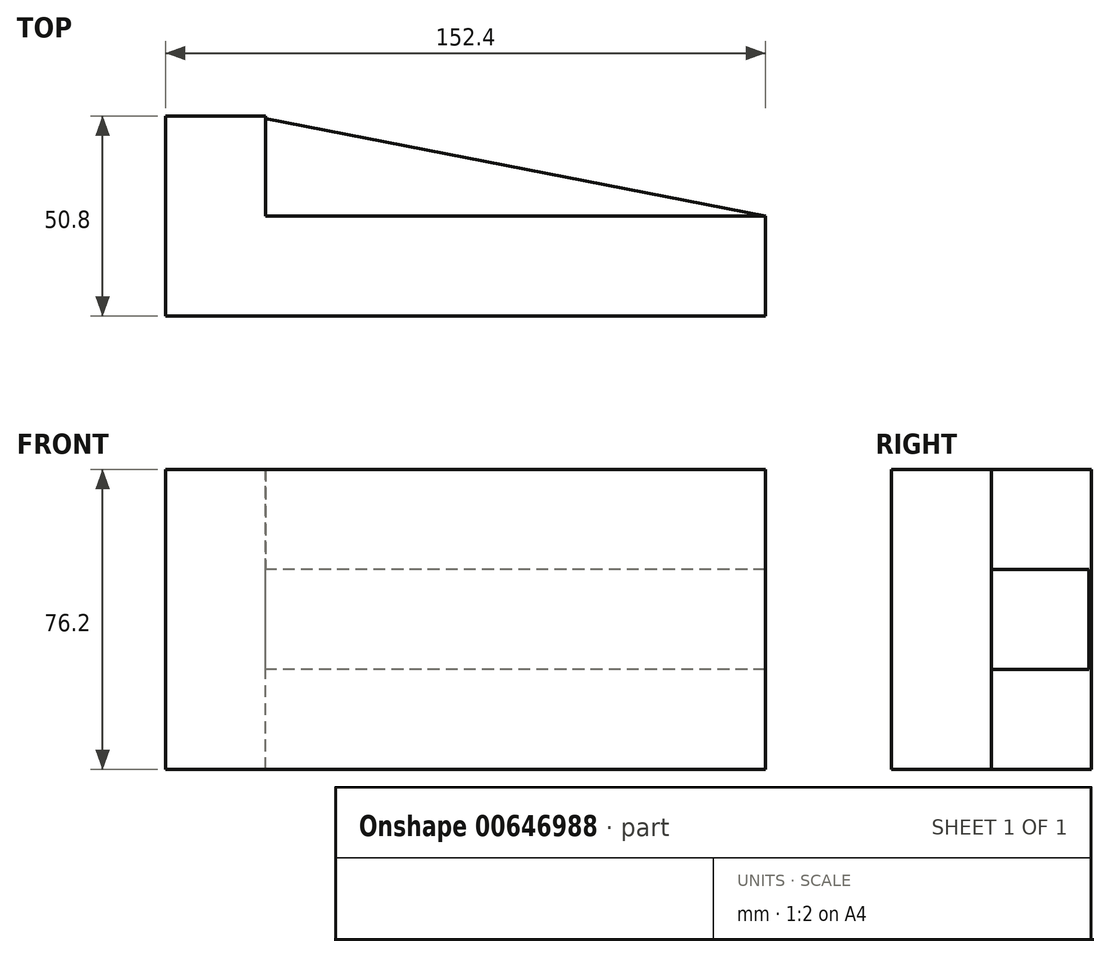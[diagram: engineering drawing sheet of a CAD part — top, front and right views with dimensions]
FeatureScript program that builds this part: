
annotation { "Feature Type Name" : "Feature", "Feature Type Description" : "" }
export const myFeature = defineFeature(function(context is Context, id is Id, definition is map)
    precondition{}
    {
        {
            var Q0;
            Q0=qCreatedBy(makeId("Top.planeOp"),FACE);
            var sketch = newSketch(context, id + "F0", { "sketchPlane" : qUnion([Q0])});
            skLineSegment(sketch, "E0", {"start": v(-62.43, 55.99) * mm, "end": v(-62.43, 5.19) * mm});
            skLineSegment(sketch, "E1", {"start": v(-62.43, 5.19) * mm, "end": v(89.97, 5.19) * mm});
            skLineSegment(sketch, "E2", {"start": v(89.97, 5.19) * mm, "end": v(89.97, 30.59) * mm});
            skLineSegment(sketch, "E3", {"start": v(89.97, 30.59) * mm, "end": v(-37.03, 30.59) * mm});
            skLineSegment(sketch, "E4", {"start": v(-37.03, 30.59) * mm, "end": v(-37.03, 55.99) * mm});
            skLineSegment(sketch, "E5", {"start": v(-37.03, 55.99) * mm, "end": v(-62.43, 55.99) * mm});
            skLineSegment(sketch, "E6", {"start": v(-37.5, 55.47) * mm, "end": v(89.97, 30.59) * mm});
            skSolve(sketch);
        }
        {
            var Q0;
            Q0=makeQuery(id+"F0.imprint","IMPRINT",FACE,{"disambiguationData":[TD([[makeQuery(id+"F0.imprint","IMPRINT",EDGE,{"derivedFrom":sQuery(id+"F0.wireOp",EDGE,"E0")}),1.0]])]});
            extrude(context, id + "F1", {"entities" : qUnion([Q0]), "oppositeDirection" : true, "depth" : 50.8 * mm, "offsetDistance" : 25.4 * mm});
        }
        {
            var Q0;
            {var subQ0=sQuery(id+"F0.wireOp",EDGE,"E3");Q0=makeQuery(id+"F0.imprint","IMPRINT",FACE,{"disambiguationData":[TD([[makeQuery(id+"F0.imprint","IMPRINT",EDGE,{"derivedFrom":subQ0}),-1.0]])]});}
            extrude(context, id + "F2", {"entities" : qUnion([Q0]), "oppositeDirection" : true, "depth" : 25.4 * mm, "offsetDistance" : 25.4 * mm});
        }
        {
            var Q0;
            Q0=makeQuery(id+"F0.imprint","IMPRINT",FACE,{"disambiguationData":[TD([[makeQuery(id+"F0.imprint","IMPRINT",EDGE,{"derivedFrom":sQuery(id+"F0.wireOp",EDGE,"E0")}),1.0]])]});
            extrude(context, id + "F3", {"entities" : qUnion([Q0]), "operationType" : NewBodyOperationType.ADD, "depth" : 25.4 * mm, "offsetDistance" : 25.4 * mm});
        }
    });
